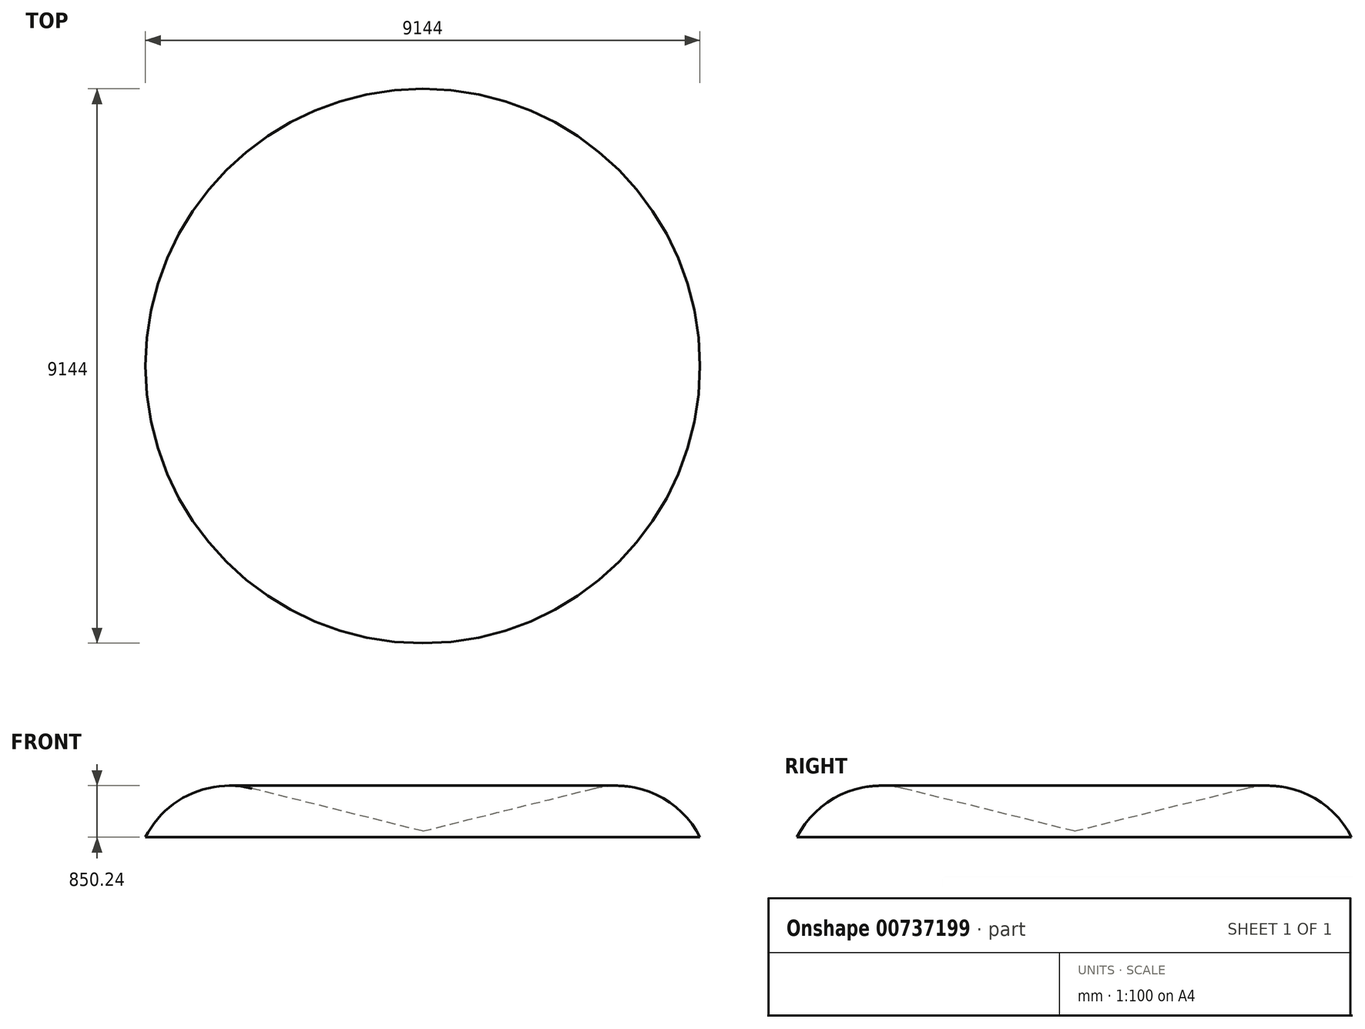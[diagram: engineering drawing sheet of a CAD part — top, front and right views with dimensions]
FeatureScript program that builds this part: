
annotation { "Feature Type Name" : "Feature", "Feature Type Description" : "" }
export const myFeature = defineFeature(function(context is Context, id is Id, definition is map)
    precondition{}
    {
        {
            var Q0;
            Q0=qCreatedBy(makeId("Front.planeOp"),FACE);
            var sketch = newSketch(context, id + "F0", { "sketchPlane" : qUnion([Q0])});
            skLineSegment(sketch, "E0", {"start": v(0, 101.6) * mm, "end": v(-2818.62, 804.36) * mm});
            skArc(sketch, "E1", {"start": v(-2818.62, 804.36) * mm, "mid": v(-3836.32, 709.56) * mm, "end": v(-4572, 0) * mm});
            skLineSegment(sketch, "E2", {"start": v(-4572, 0) * mm, "end": v(0, 0) * mm});
            skLineSegment(sketch, "E3", {"start": v(-3192.29, -694.33) * mm, "end": v(0, 101.6) * mm, "construction": true});
            skLineSegment(sketch, "E4", {"start": v(0, 101.6) * mm, "end": v(0, 0) * mm});
            skSolve(sketch);
        }
        {
            var Q0;
            Q0=qCreatedBy(makeId("Front.planeOp"),FACE);
            var sketch = newSketch(context, id + "F1", { "sketchPlane" : qUnion([Q0])});
            skLineSegment(sketch, "E5", {"start": v(0, 0) * mm, "end": v(0, 263.23) * mm});
            skSolve(sketch);
        }
        {
            var Q0;
            Q0=makeQuery(id+"F0.imprint","IMPRINT",FACE,{"disambiguationData":[TD([[makeQuery(id+"F0.imprint","IMPRINT",EDGE,{"derivedFrom":sQuery(id+"F0.wireOp",EDGE,"E0")}),1.0]])]});
            var Q1;
            Q1=sQuery(id+"F1.wireOp",EDGE,"E5");
            revolve(context, id + "F2", {"surfaceOperationType" : NewSurfaceOperationType.NEW, "entities" : qUnion([Q0]), "axis" : qUnion([Q1]), "revolveType" : RevolveType.FULL});
        }
    });
